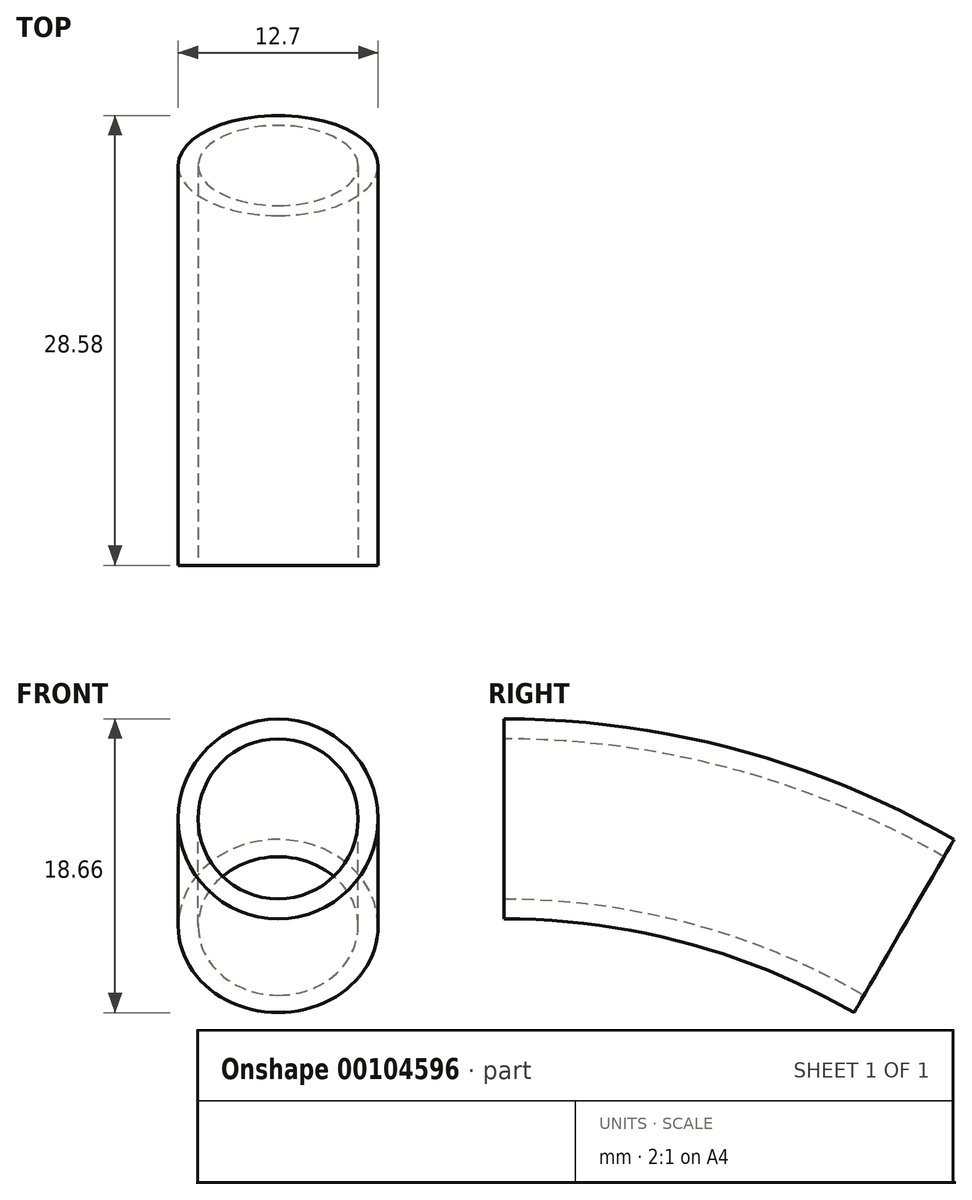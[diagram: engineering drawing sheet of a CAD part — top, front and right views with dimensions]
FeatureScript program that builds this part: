
annotation { "Feature Type Name" : "Feature", "Feature Type Description" : "" }
export const myFeature = defineFeature(function(context is Context, id is Id, definition is map)
    precondition{}
    {
        {
            var Q0;
            Q0=qCreatedBy(makeId("Front.planeOp"),FACE);
            var sketch = newSketch(context, id + "F0", { "sketchPlane" : qUnion([Q0])});
            skCircle(sketch, "E0", {"center": v(0, 0) * mm, "radius": 6.35 * mm});
            skCircle(sketch, "E1", {"center": v(0, 0) * mm, "radius": 5.08 * mm});
            skSolve(sketch);
        }
        {
            var Q0;
            Q0=qCreatedBy(makeId("Right.planeOp"),FACE);
            var sketch = newSketch(context, id + "F1", { "sketchPlane" : qUnion([Q0])});
            skArc(sketch, "E2", {"start": v(25.4, -6.8) * mm, "mid": v(13.15, -1.73) * mm, "end": v(0, 0) * mm});
            skPoint(sketch, "E3.orphan", {"position": v(0, -101.6) * mm});
            skSolve(sketch);
        }
        {
            var Q0;
            Q0=makeQuery(id+"F0.imprint","IMPRINT",FACE,{"disambiguationData":[TD([[makeQuery(id+"F0.imprint","IMPRINT",EDGE,{"derivedFrom":sQuery(id+"F0.wireOp",EDGE,"E0")}),1.0]])]});
            var Q1;
            Q1=sQuery(id+"F1.wireOp",EDGE,"E2");
            sweep(context, id + "F2", {"profiles" : qUnion([Q0]), "path" : qUnion([Q1])});
        }
    });
